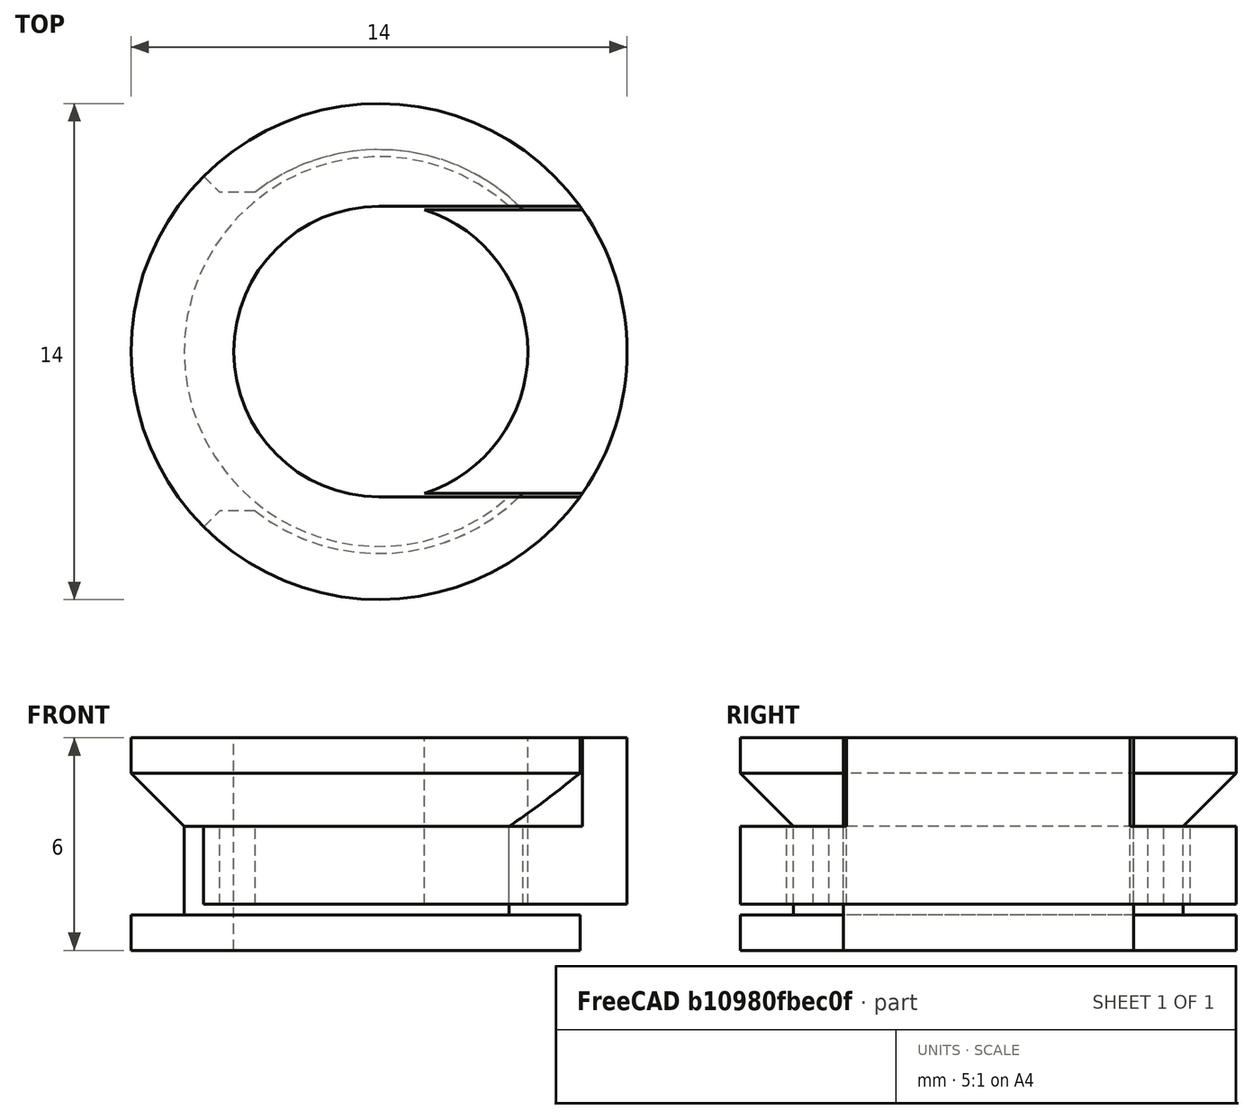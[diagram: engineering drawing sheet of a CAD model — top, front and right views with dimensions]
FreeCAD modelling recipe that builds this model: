
FCSTD DOCUMENT  (FreeCAD 0.18R14555 (Git shallow))
Label: z-cover
License: All rights reserved
LicenseURL: http://en.wikipedia.org/wiki/All_rights_reserved
objects: Part::Cut×10, Part::Cylinder×9, Part::Box×5, Part::Chamfer×2, Part::MultiCommon×1, Part::MultiFuse×1
note: 28 computed .brp shape members not serialized (recipe doc carries the construction recipe); baked Part::Feature solids carry a one-line shape summary decoded from their .brp

FEATURE [Part::Cylinder] Cylinder
  Angle = 360
  AttacherType = Attacher::AttachEngine3D
  Height = 6
  Radius = 7
FEATURE [Part::Cylinder] Cylinder001
  Angle = 360
  AttacherType = Attacher::AttachEngine3D
  Height = 6
  Radius = 4.1
FEATURE [Part::Cut] Cut
  Base = -> Cylinder
  Tool = -> Cylinder001
FEATURE [Part::Cylinder] Cylinder002
  Angle = 360
  AttacherType = Attacher::AttachEngine3D
  Height = 4
  Placement = pos=(0,0,1) rot=(0,0,1;0rad)
  Radius = 8
FEATURE [Part::Cylinder] Cylinder003
  Angle = 360
  AttacherType = Attacher::AttachEngine3D
  Height = 4
  Placement = pos=(0,0,1) rot=(0,0,1;0rad)
  Radius = 5.5
FEATURE [Part::Box] Box  label="Cube"
  AttacherType = Attacher::AttachEngine3D
  Height = 10
  Length = 12
  Placement = pos=(0,-4.1,0) rot=(0,0,1;0rad)
  Width = 8.2
FEATURE [Part::Box] Box001  label="Cube001"
  AttacherType = Attacher::AttachEngine3D
  Height = 6
  Length = 8
  Placement = pos=(0,-4,0) rot=(0,0,1;0rad)
  Width = 8
FEATURE [Part::Cylinder] Cylinder009
  Angle = 360
  AttacherType = Attacher::AttachEngine3D
  Height = 10
  Radius = 7
FEATURE [Part::MultiCommon] Common001
  Shapes = -> [Cylinder009,Box001]
FEATURE [Part::Cylinder] Cylinder010
  Angle = 360
  AttacherType = Attacher::AttachEngine3D
  Height = 10
  Radius = 4.2
FEATURE [Part::Cylinder] Cylinder011
  Angle = 360
  AttacherType = Attacher::AttachEngine3D
  Height = 1.3
  Radius = 10
FEATURE [Part::Box] Box002  label="Cube002"
  AttacherType = Attacher::AttachEngine3D
  Height = 6
  Length = 10
  Placement = pos=(-10,-4,0) rot=(0,0,1;0rad)
  Width = 8
FEATURE [Part::Box] Box003  label="Cube003"
  AttacherType = Attacher::AttachEngine3D
  Height = 10
  Length = 10
  Placement = pos=(-13.5,-7,0) rot=(0,0,1;0rad)
  Width = 14
FEATURE [Part::Chamfer] Chamfer002
  Base = -> Box003
  Edges = 2 edges r=3: [Edge5,Edge7]
  Placement = pos=(-0.5,0,0) rot=(0,0,1;0rad)
FEATURE [Part::Box] Box004  label="Cube004"
  AttacherType = Attacher::AttachEngine3D
  Height = 10
  Length = 10
  Placement = pos=(-10,-4.5,1) rot=(0,0,1;0rad)
  Width = 9
FEATURE [Part::Cut] Cut010
  Base = -> Cylinder002
  Tool = -> Cylinder003
FEATURE [Part::Chamfer] Chamfer
  Base = -> Cut010
  Edges = 1 edges r=1.5: [Edge4]
FEATURE [Part::Cut] Cut011
  Base = -> Cut
  Tool = -> Chamfer
FEATURE [Part::Cut] Cut012
  Base = -> Cut011
  Tool = -> Box
FEATURE [Part::Cut] Cut014
  Base = -> Common001
  Tool = -> Cylinder010
FEATURE [Part::Cylinder] Cylinder013
  Angle = 360
  AttacherType = Attacher::AttachEngine3D
  Height = 2.3
  Placement = pos=(0,0,1.2) rot=(0,0,1;0rad)
  Radius = 7
FEATURE [Part::Cylinder] Cylinder014
  Angle = 360
  AttacherType = Attacher::AttachEngine3D
  Height = 10
  Placement = pos=(0,0,1.2) rot=(0,0,1;0rad)
  Radius = 5.7
FEATURE [Part::Cut] Cut015
  Base = -> Cylinder013
  Tool = -> Cylinder014
FEATURE [Part::MultiFuse] Fusion
  Shapes = -> [Cut014,Cut015]
FEATURE [Part::Cut] Cut016
  Base = -> Fusion
  Tool = -> Cylinder011
FEATURE [Part::Cut] Cut017
  Base = -> Cut016
  Tool = -> Box002
FEATURE [Part::Cut] Cut018
  Base = -> Cut017
  Tool = -> Chamfer002
FEATURE [Part::Cut] Cut019
  Base = -> Cut018
  Tool = -> Box004
